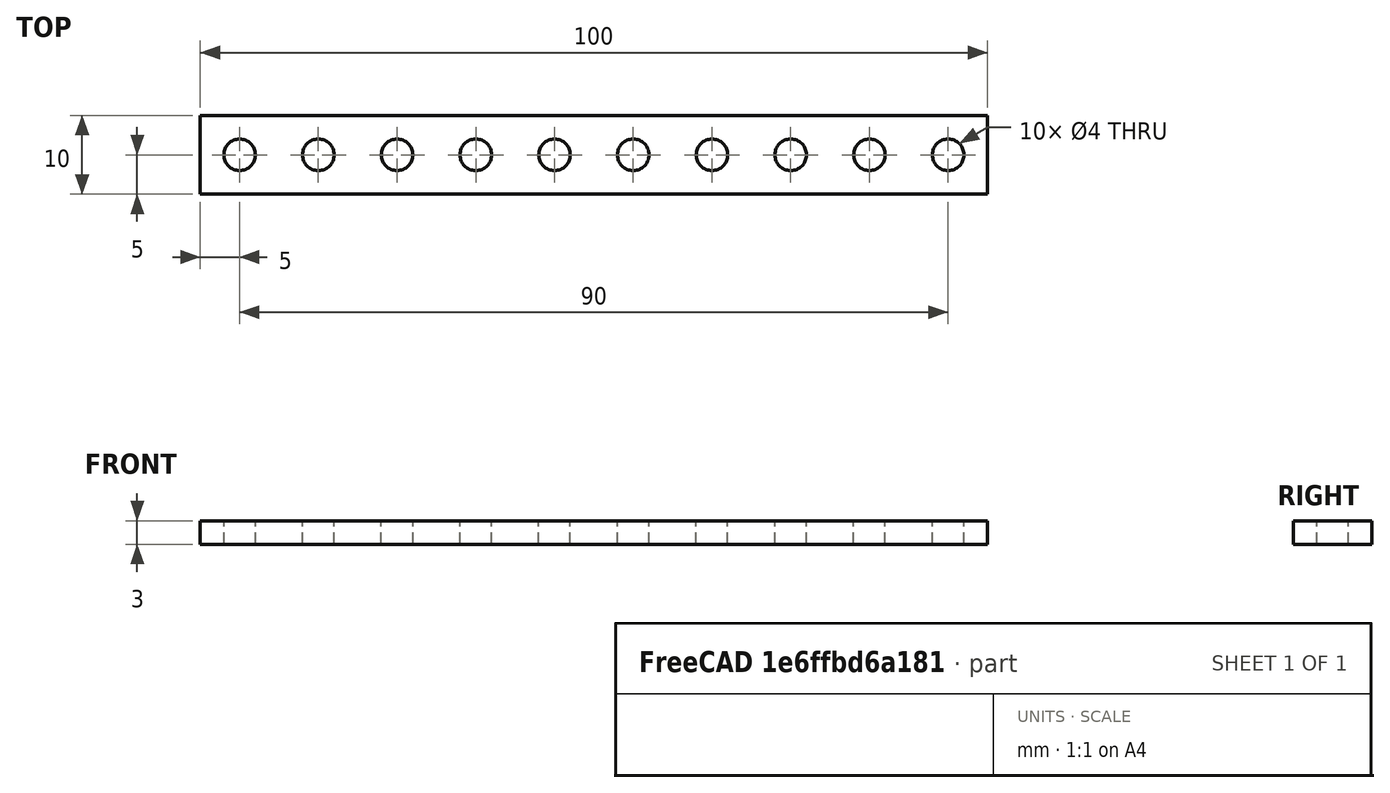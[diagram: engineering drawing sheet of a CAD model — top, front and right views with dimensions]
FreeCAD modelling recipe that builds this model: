
FCSTD DOCUMENT  (FreeCAD 0.17R13217 (Git))
Label: 11-pieza-mecano-10
License: All rights reserved
LicenseURL: http://en.wikipedia.org/wiki/All_rights_reserved
objects: Part::Cylinder×1, Part::FeaturePython×1, Part::Box×1, Part::Cut×1
note: 4 computed .brp shape members not serialized (recipe doc carries the construction recipe); baked Part::Feature solids carry a one-line shape summary decoded from their .brp

FEATURE [Part::Cylinder] Cylinder  label="Cilindro"
  Angle = 360
  AttacherType = Attacher::AttachEngine3D
  Height = 10
  Placement = pos=(0,0,-5) rot=(0,0,1;0rad)
  Radius = 2
FEATURE [Part::FeaturePython] Array  # Draft array (typed FeaturePython)
  Angle = 360
  ArrayType = 0
  Axis = (0,0,1)
  Base = -> Cylinder
  Center = (0,0,0)
  Fuse = true
  IntervalAxis = (0,0,0)
  IntervalX = (10,0,0)
  IntervalY = (0,10,0)
  IntervalZ = (0,0,0)
  NumberPolar = 1
  NumberX = 10
  NumberY = 1
  NumberZ = 1
FEATURE [Part::Box] Box  label="Cubo"
  AttacherType = Attacher::AttachEngine3D
  Height = 3
  Length = 100
  Placement = pos=(-5,-5,0) rot=(0,0,1;0rad)
  Width = 10
FEATURE [Part::Cut] Cut
  Base = -> Box
  Refine = true
  Tool = -> Array
